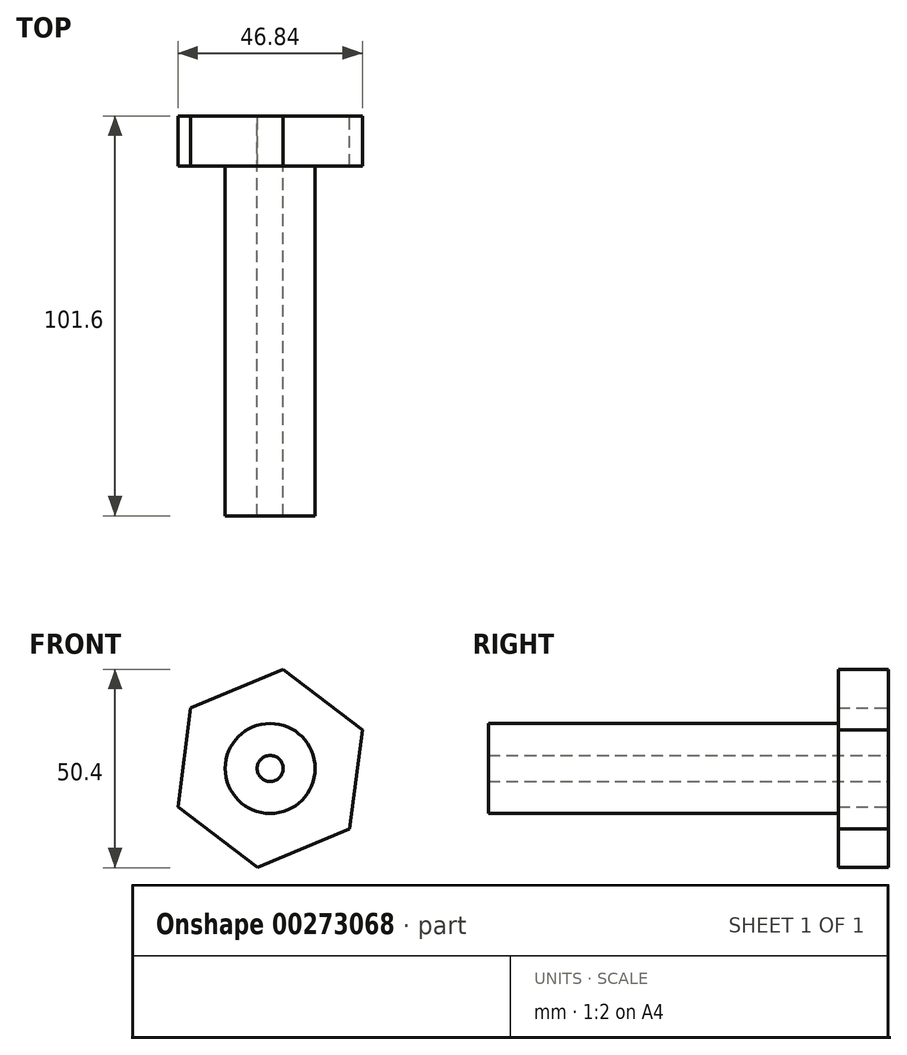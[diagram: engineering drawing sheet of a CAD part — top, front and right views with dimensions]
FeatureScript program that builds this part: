
annotation { "Feature Type Name" : "Feature", "Feature Type Description" : "" }
export const myFeature = defineFeature(function(context is Context, id is Id, definition is map)
    precondition{}
    {
        {
            var Q0;
            Q0=qCreatedBy(makeId("Front.planeOp"),FACE);
            var sketch = newSketch(context, id + "F0", { "sketchPlane" : qUnion([Q0])});
            skCircle(sketch, "E0.cCircle", {"center": v(0, 0) * mm, "radius": 22 * mm, "construction": true});
            skLineSegment(sketch, "E0.0", {"start": v(-20.22, 15.37) * mm, "end": v(3.2, 25.2) * mm});
            skLineSegment(sketch, "E0.1", {"start": v(3.2, 25.2) * mm, "end": v(23.42, 9.82) * mm});
            skLineSegment(sketch, "E0.2", {"start": v(23.42, 9.82) * mm, "end": v(20.22, -15.37) * mm});
            skLineSegment(sketch, "E0.3", {"start": v(20.22, -15.37) * mm, "end": v(-3.2, -25.2) * mm});
            skLineSegment(sketch, "E0.4", {"start": v(-3.2, -25.2) * mm, "end": v(-23.42, -9.82) * mm});
            skLineSegment(sketch, "E0.5", {"start": v(-23.42, -9.82) * mm, "end": v(-20.22, 15.37) * mm});
            skPoint(sketch, "E0.0.midPoint", {"position": v(-8.5, 20.29) * mm});
            skSolve(sketch);
        }
        {
            var Q0;
            Q0=makeQuery(id+"F0.imprint","IMPRINT",FACE,{"disambiguationData":[TD([[makeQuery(id+"F0.imprint","IMPRINT",EDGE,{"derivedFrom":sQuery(id+"F0.wireOp",EDGE,"E0.0")}),-1.0]])]});
            extrude(context, id + "F1", {"entities" : qUnion([Q0]), "depth" : 12.7 * mm});
        }
        {
            var Q0;
            Q0=qCreatedBy(makeId("Front.planeOp"),FACE);
            var sketch = newSketch(context, id + "F2", { "sketchPlane" : qUnion([Q0])});
            skCircle(sketch, "E1", {"center": v(0, 0) * mm, "radius": 11.43 * mm});
            skSolve(sketch);
        }
        {
            var Q0;
            Q0=makeQuery(id+"F2.imprint","IMPRINT",FACE,{"disambiguationData":[TD([[makeQuery(id+"F2.imprint","IMPRINT",EDGE,{"derivedFrom":sQuery(id+"F2.wireOp",EDGE,"E1")}),1.0]])]});
            extrude(context, id + "F3", {"entities" : qUnion([Q0]), "operationType" : NewBodyOperationType.ADD, "depth" : 101.6 * mm});
        }
        {
            var Q0;
            Q0=qCreatedBy(makeId("Front.planeOp"),FACE);
            var sketch = newSketch(context, id + "F4", { "sketchPlane" : qUnion([Q0])});
            skCircle(sketch, "E2", {"center": v(0, 0) * mm, "radius": 3.3 * mm});
            skSolve(sketch);
        }
        {
            var Q0;
            Q0=makeQuery(id+"F4.imprint","IMPRINT",FACE,{"disambiguationData":[TD([[makeQuery(id+"F4.imprint","IMPRINT",EDGE,{"derivedFrom":sQuery(id+"F4.wireOp",EDGE,"E2")}),1.0]])]});
            extrude(context, id + "F5", {"entities" : qUnion([Q0]), "depth" : 101.6 * mm});
        }
    });
